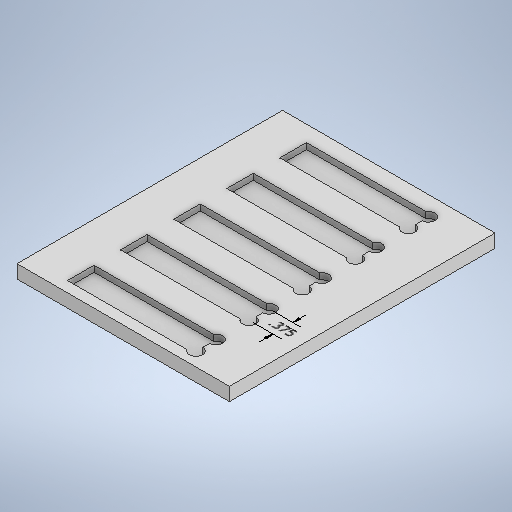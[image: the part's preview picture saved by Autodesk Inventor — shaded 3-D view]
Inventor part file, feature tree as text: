
AUTODESK INVENTOR PART (.ipt)
format: ipt  version: 2025.3 (Build 293356030, 356C)  size: 282,112 bytes
history: native  units: in
note: dims shown in document units (in); Inventor stores cm internally (conversion verified against a paired STEP export)
features: sketch x3, other x2, extrude x2
ambient origin geometry x8: Origin, YZ Plane, XZ Plane, XY Plane, X Axis, Y Axis, Z Axis, Center Point
bodies: Solid1 (feature_tree)
feature tree (7):
  other  "Annotations"
  extrude  "Extrusion1"  Depth=5.0in
  extrude  "Extrusion2"  Depth=0.5in
  sketch  "Sketch1"  dims[d0=4.0in d1=5.0in]
  sketch  "Sketch2"  dims[d6=0.25in d7=0.25in d8=0.125in d9=2.25in d10=0.75in d11=0.2in d12=1.9685in d14=1.0in d15=0.3937in d17=1.0in d19=0.115in d20=0.0in d21=0.3747in]
  sketch  "Sketch Rectangular Pattern1"  dims[d2=0.25in d3=0.0in d5=0.5in]
  other  "Linear Dimension 1"
